# Revit family: Spannbügel VA
name_source: partatom
category: HLS-Bauteile
revit_build: Autodesk Revit 2017 (Build: 20190507_1515(x64)
units: mm (PartAtom-declared; Revit-internal decimal feet)

## family parameters
Arbeitsebenenbasiert = Ja
Beim Laden mit Abzugskörper schneiden = Nein
Bemaßung runder Anschluss = Durchmesser verwenden
Gemeinsam genutzt = Ja
Immer vertikal = Nein
Raumberechnungspunkt = Nein
Teiletyp = Normal

## types (2) — shared parameters
Achsabstand U-Bügel = 56 mm
B1 = 56 mm  [stored 0.183727 ft]
Breite Spannwinkel = 80 mm
Fabrikat = MEFA
Firma = MEFA Befestigungs- und Montagesysteme GmbH
Flachscheibe = Unterlegscheibe VA : Unterlegscheibe 10,5x20x2,0 V4A
Klemmdicke = 26 mm
Kurztext1 = Spannbügel M10 45 V4A
Material = Edelstahl
Mutter = Sechskantmutter VA : Sechskantmutter M10 V4A
Profiltyp = 45
S = 6 mm  [stored 0.019685 ft]
Spanwinkel = Spannwinkel VA : Spanwinkel 80/20/6 VA
Vorgabe-Ansicht = 1219 mm
max. zul. Last Fx = 0.00 kN
max. zul. Last Fy = 0.00 kN
max. zul. Last Fz = 0.00 kN
min. Randabstand = 70 mm  [stored 0.229659 ft]

## per-type parameters (varying)
| type | Artikelnummer | EAN | Gewicht | Gewicht pro Bauteil | Kurztext2 | L | Länge U-Bügel | Rundstahl |
| Spannbügel M10 45- 60, V4A | 0481690 | 4250928459107 | 0.40 kg | 0.40 kg | Profilhöhe 26 - 45 mm Klemmdicke 26 mm | 75 mm | 90 mm | Rundstahl U-Bügel VA : Rundstahl U Bügel 56- 90 M10 VA |
| Spannbügel M10 45- 90, V4A | 0481692 | 4250928459114 | 0.45 kg | 0.45 kg | Profilhöhe 90 mm Klemmdicke 26 mm | 110 mm  [stored 0.360892 ft] | 135 mm | Rundstahl U-Bügel VA : Rundstahl U Bügel 56-135 M10 VA |

note: [stored X ft] marks values corroborated as IEEE doubles in the binary element streams (Revit-internal decimal feet)

## geometry (parser evidence)
native form markers: Sweep x3
no freeform markers — native parametric forms only
